# Revit family: QF_BPRO_CCE-V 54-33_574928
name_source: partatom
category: Sonderausstattung
revit_build: Autodesk Revit 2018 (Build: 20190510_1515(x64)
units: mm (PartAtom-declared; Revit-internal decimal feet)

## family parameters
Arbeitsebenenbasiert = Nein
Beim Laden mit Abzugskörper schneiden = Nein
Bemaßung runder Anschluss = Durchmesser verwenden
Gemeinsam genutzt = Nein
Immer vertikal = Ja
Raumberechnungspunkt = Ja
Teiletyp = Normal

## types (1)
- CCE-V 54-33
    Artikel Nummer = 574928
    Beschreibung = Tablettspender, offene Ausführung;
für Tabletts im GN-Format 530x325 mm
ca. 100 Tabletts;
    Beschreibung durch Hersteller analog Leistungsverzeichniskurztext = CCE-V 54/33 – Tablettspender 


Abmessungen

Länge:					810 mm
Breite:					555 mm
Höhe:					900 mm


Ausführung

Aufbau

Der Korpus besteht komplett aus CNS 18/10. Die Oberfläche ist mikroliert. Der Tablettspender ist offen ausgeführt. Die Tabletts werden auf eine Plattform aufgesetzt. Diese ist dreiseitig aufgekantet (nicht an den Ecken wegen der Reinigung), um das Verrutschen der Tabletts zu vermeiden. Nach vorne hin ist die Plattform offen. Die Tabletts werden längs abgestapelt. Durch Ein- bzw. Aushängen der Zugfedern kann die Federspannung entsprechend dem Stapelgut reguliert werden, um eine gleichbleibende Ausgabehöhe zu gewährleisten.


Einsatz/Ergonomie

Der verstärkte Tablettspender ist speziell für das Abstapeln der Heißluft-Tabletts des B.PRO
    Beschreibung durch Hersteller analog Leistungsverzeichnislangtext = CCE-V 54/33 – Tablettspender 


Abmessungen

Länge:					810 mm
Breite:					555 mm
Höhe:					900 mm


Ausführung

Aufbau

Der Korpus besteht komplett aus CNS 18/10. Die Oberfläche ist mikroliert. Der Tablettspender ist offen ausgeführt. Die Tabletts werden auf eine Plattform aufgesetzt. Diese ist dreiseitig aufgekantet (nicht an den Ecken wegen der Reinigung), um das Verrutschen der Tabletts zu vermeiden. Nach vorne hin ist die Plattform offen. Die Tabletts werden längs abgestapelt. Durch Ein- bzw. Aushängen der Zugfedern kann die Federspannung entsprechend dem Stapelgut reguliert werden, um eine gleichbleibende Ausgabehöhe zu gewährleisten.


Einsatz/Ergonomie

Der verstärkte Tablettspender ist speziell für das Abstapeln der Heißluft-Tabletts des B.PRO
    Gerätegewicht Netto = 41.00 kg
    Großküchengerätezuordnung = Ja
    Hersteller = B.PRO GmbH
    Höhe = 900 mm  [stored 2.95276 ft]
    Internetadresse Gerätehersteller = https://www.bpro-solutions.com
    Internetadresse für Ersatzteilliste = https://www.bpro-solutions.com
    Kosten = 1837.2 $
    Länge Gerätebreite = 810 mm
    Länge Tablettträger = 540 mm  [stored 1.77165 ft]
    Länge Tragarm = 512 mm  [stored 1.67979 ft]
    Material = QF_Metal-Stainless-Steel_general
    Material_Stoßschutz = QF_Rubber-Black-Matt
    Modell = CCE-V 54-33
    Sockelhöhe = 160 mm  [stored 0.524934 ft]
    Tablettträger OK = 575 mm
    Tiefe = 555 mm  [stored 1.82087 ft]
    Tiefe Tablettträger = 335 mm  [stored 1.09908 ft]
    Typenkommentare = Tablettspender, offen, im GN-Format
    URL = https://www.bpro-solutions.com
    Warnhinweise = Ausführliche Gefahrenhinweise entnehmen Sie der Betriebsanleitung.
    Zubehör = Nein

note: [stored X ft] marks values corroborated as IEEE doubles in the binary element streams (Revit-internal decimal feet)
